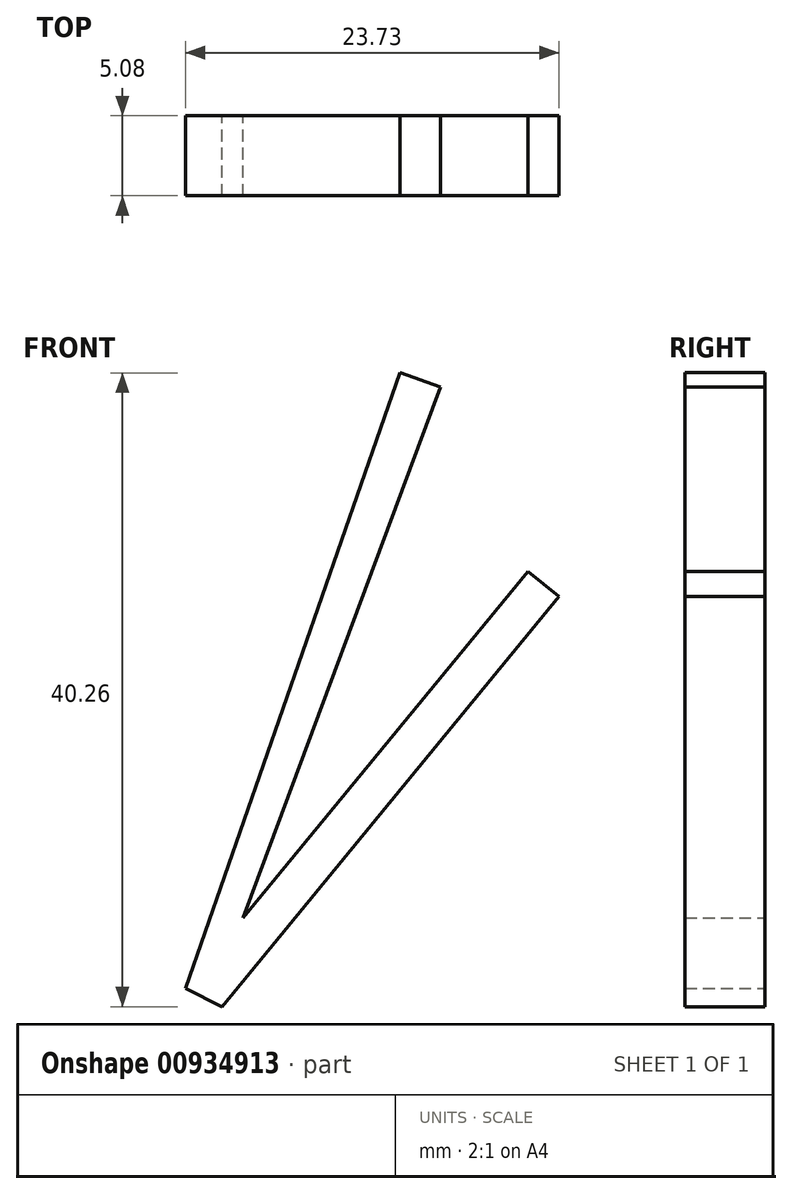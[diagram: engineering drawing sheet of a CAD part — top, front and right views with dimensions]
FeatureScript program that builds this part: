
annotation { "Feature Type Name" : "Feature", "Feature Type Description" : "" }
export const myFeature = defineFeature(function(context is Context, id is Id, definition is map)
    precondition{}
    {
        {
            var Q0;
            Q0=qCreatedBy(makeId("Front.planeOp"),FACE);
            var sketch = newSketch(context, id + "F0", { "sketchPlane" : qUnion([Q0])});
            skLineSegment(sketch, "E0", {"start": v(0, 0) * mm, "end": v(21.39, 26.04) * mm});
            skLineSegment(sketch, "E1", {"start": v(21.39, 26.04) * mm, "end": v(19.42, 27.66) * mm});
            skLineSegment(sketch, "E2", {"start": v(19.42, 27.66) * mm, "end": v(-2.34, 1.17) * mm});
            skLineSegment(sketch, "E3", {"start": v(-2.34, 1.17) * mm, "end": v(0, 0) * mm});
            skLineSegment(sketch, "E4", {"start": v(-2.34, 1.17) * mm, "end": v(11.28, 40.26) * mm});
            skLineSegment(sketch, "E5", {"start": v(11.28, 40.26) * mm, "end": v(13.87, 39.36) * mm});
            skLineSegment(sketch, "E6", {"start": v(13.87, 39.36) * mm, "end": v(1.33, 5.63) * mm});
            skSolve(sketch);
        }
        {
            var Q0;
            {var subQ0=sQuery(id+"F0.wireOp",EDGE,"E4");Q0=makeQuery(id+"F0.imprint","IMPRINT",FACE,{"disambiguationData":[TD([[makeQuery(id+"F0.imprint","IMPRINT",EDGE,{"derivedFrom":subQ0}),-1.0]])]});}
            var Q1;
            Q1=makeQuery(id+"F0.imprint","IMPRINT",FACE,{"disambiguationData":[TD([[makeQuery(id+"F0.imprint","IMPRINT",EDGE,{"derivedFrom":sQuery(id+"F0.wireOp",EDGE,"E0")}),1.0]])]});
            extrude(context, id + "F1", {"entities" : qUnion([Q0, Q1]), "depth" : 5.08 * mm, "offsetDistance" : 25.4 * mm});
        }
    });
